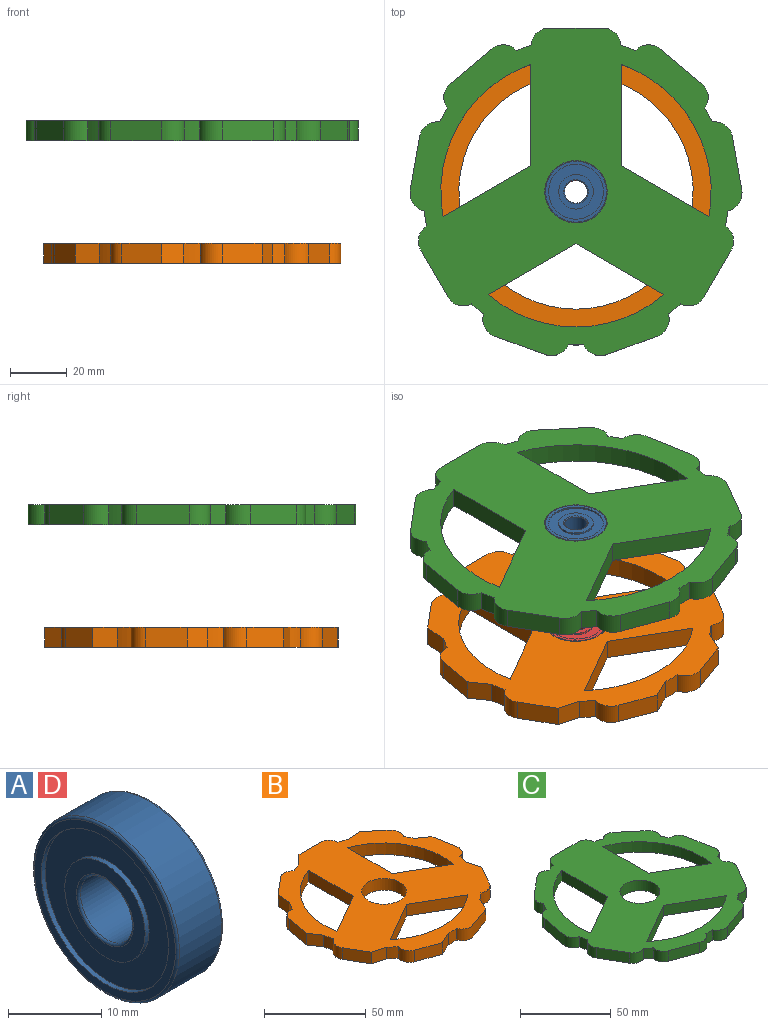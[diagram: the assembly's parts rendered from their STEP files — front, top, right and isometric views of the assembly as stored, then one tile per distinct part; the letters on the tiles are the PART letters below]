
ASSEMBLY  parts=4 mates=5
PART A: 16 faces, bbox 7x23.8x23.8 mm
  f0: torus R=10.7mm, axis (1,0,0), area 32.2mm2, adj f1,f15
  f1: plane 21.4x21.4mm, normal (-1,0,0), area 67.1mm2, adj f0,f2
  f2: cylinder r=9.65mm len=19.3mm, axis (1,0,0), area 36.4mm2, adj f1,f3
  f3: plane 19.3x19.3mm, normal (-1,0,0), area 175.7mm2, adj f2,f4
  f4: cylinder r=6.1mm len=12.2mm, axis (1,0,0), area 23mm2, adj f3,f5
  f5: plane 12.2x12.2mm, normal (-1,0,0), area 58.8mm2, adj f4,f6
  f6: torus R=4.3mm, axis (1,0,0), area 12.2mm2, adj f5,f7
  f7: cylinder r=4mm len=8mm, axis (1,0,0), area 160.8mm2, adj f6,f8
  f8: torus R=4.3mm, axis (1,0,0), area 12.2mm2, adj f7,f9
  f9: plane 12.2x12.2mm, normal (1,0,0), area 58.8mm2, adj f8,f10
  f10: cylinder r=6.1mm len=12.2mm, axis (1,0,0), area 23mm2, adj f9,f11
  f11: plane 19.3x19.3mm, normal (1,0,0), area 175.7mm2, adj f10,f12
  f12: cylinder r=9.65mm len=19.3mm, axis (1,0,0), area 36.4mm2, adj f11,f13
  f13: plane 21.4x21.4mm, normal (1,0,0), area 67.1mm2, adj f12,f14
  f14: torus R=10.7mm, axis (1,0,0), area 32.2mm2, adj f13,f15
  f15: cylinder r=11mm len=22mm, axis (1,0,0), area 442.3mm2, adj f0,f14
PART B: 48 faces, bbox 104.6x103.3x7 mm
  f0: plane 7.82x7mm, normal (0.91,-0.42,0), area 60.4mm2, adj f1,f41,f46,f47
  f1: cylinder r=47.62mm len=7mm, axis (0,0,-1), area 40.2mm2, adj f0,f2,f46,f47
  f2: cylinder r=6.1mm len=8.33mm, axis (0,0,-1), area 67.1mm2, adj f1,f3,f46,f47
  f3: plane 12.93x7.46mm, normal (0.87,-0.5,0), area 104.5mm2, adj f2,f4,f46,f47
  f4: plane 8.33x7mm, normal (0.97,0.26,0), area 60.4mm2, adj f3,f5,f46,f47
  f5: cylinder r=47.62mm len=7mm, axis (0,0,-1), area 40.2mm2, adj f4,f6,f46,f47
  f6: cylinder r=6.1mm len=7.07mm, axis (0,0,-1), area 67.1mm2, adj f5,f7,f46,f47
  f7: plane 14.7x7mm, normal (0.98,0.17,0), area 104.5mm2, adj f6,f8,f46,f47
  f8: plane 7.07x7mm, normal (0.57,0.82,0), area 60.4mm2, adj f7,f9,f46,f47
  f9: cylinder r=47.62mm len=7mm, axis (0,0,-1), area 40.2mm2, adj f8,f10,f46,f47
  f10: cylinder r=6.1mm len=8.59mm, axis (0,0,-1), area 67.1mm2, adj f9,f11,f46,f47
  f11: plane 11.44x9.6mm, normal (0.64,0.77,0), area 104.5mm2, adj f10,f12,f46,f47
  f12: plane 8.59x7mm, normal (-0.09,1,0), area 60.4mm2, adj f11,f13,f46,f47
  f13: cylinder r=47.62mm len=7mm, axis (0,0,-1), area 40.2mm2, adj f12,f14,f46,f47
  f14: cylinder r=6.1mm len=7mm, axis (0,0,-1), area 67.1mm2, adj f13,f15,f46,f47
  f15: plane 14.93x7mm, normal (0,1,0), area 104.5mm2, adj f14,f16,f46,f47
  f16: plane 7x6.1mm, normal (-0.71,0.71,0), area 60.4mm2, adj f15,f17,f46,f47
  f17: cylinder r=47.62mm len=7mm, axis (0,0,-1), area 40.2mm2, adj f16,f18,f46,f47
  f18: cylinder r=6.1mm len=8.59mm, axis (0,0,-1), area 67.1mm2, adj f17,f19,f46,f47
  f19: plane 11.44x9.6mm, normal (-0.64,0.77,0), area 104.5mm2, adj f18,f20,f46,f47
  f20: plane 8.59x7mm, normal (-1,0.09,0), area 60.4mm2, adj f19,f21,f46,f47
  f21: cylinder r=47.62mm len=7mm, axis (0,0,-1), area 40.2mm2, adj f20,f22,f46,f47
  f22: cylinder r=6.1mm len=7.07mm, axis (0,0,-1), area 67.1mm2, adj f21,f23,f46,f47
  f23: plane 14.7x7mm, normal (-0.98,0.17,0), area 104.5mm2, adj f22,f24,f46,f47
  f24: plane 7.07x7mm, normal (-0.82,-0.57,0), area 60.4mm2, adj f23,f25,f46,f47
  f25: cylinder r=47.62mm len=7mm, axis (0,0,-1), area 40.2mm2, adj f24,f26,f46,f47
  f26: cylinder r=6.1mm len=8.33mm, axis (0,0,-1), area 67.1mm2, adj f25,f27,f46,f47
  f27: plane 12.93x7.46mm, normal (-0.87,-0.5,0), area 104.5mm2, adj f26,f28,f46,f47
  f28: plane 8.33x7mm, normal (-0.26,-0.97,0), area 60.4mm2, adj f27,f29,f46,f47
  f29: cylinder r=47.62mm len=7mm, axis (0,0,-1), area 40.2mm2, adj f28,f30,f46,f47
  f30: cylinder r=6.1mm len=7.82mm, axis (0,0,-1), area 67.1mm2, adj f29,f31,f46,f47
  f31: plane 14.03x7mm, normal (-0.34,-0.94,0), area 104.5mm2, adj f30,f32,f46,f47
  f32: plane 7.82x7mm, normal (0.42,-0.91,0), area 60.4mm2, adj f31,f33,f46,f47
  f33: cylinder r=47.62mm len=7mm, axis (0,0,-1), area 40.2mm2, adj f32,f34,f46,f47
  f34: cylinder r=6.1mm len=7.82mm, axis (0,0,-1), area 67.1mm2, adj f33,f41,f46,f47
  f35: plane 26.98x15.58mm, normal (-0.5,0.87,0), area 218.1mm2, adj f36,f42,f46,f47
  f36: cylinder r=41.27mm len=46.73mm, axis (0,0,-1), area 411.6mm2, adj f35,f42,f46,f47
  f37: cylinder r=41.27mm len=53.96mm, axis (0,0,-1), area 411.6mm2, adj f38,f43,f46,f47
  f38: plane 26.98x15.58mm, normal (0.5,-0.87,0), area 218.1mm2, adj f37,f43,f46,f47
  f39: cylinder r=41.27mm len=46.73mm, axis (0,0,-1), area 411.6mm2, adj f40,f44,f46,f47
  f40: plane 26.98x15.58mm, normal (0.5,0.87,0), area 218.1mm2, adj f39,f44,f46,f47
  f41: plane 14.03x7mm, normal (0.34,-0.94,0), area 104.5mm2, adj f0,f34,f46,f47
  f42: plane 31.15x7mm, normal (-1,0,0), area 218.1mm2, adj f35,f36,f46,f47
  f43: plane 26.98x15.58mm, normal (-0.5,-0.87,0), area 218.1mm2, adj f37,f38,f46,f47
  f44: plane 31.15x7mm, normal (1,0,0), area 218.1mm2, adj f39,f40,f46,f47
  f45: cylinder r=11mm len=22mm, axis (0,0,-1), area 483.8mm2, adj f46,f47
  f46: plane 104.62x103.3mm, normal (0,0,1), area 5299.8mm2, adj f0,f1,f2,f3,f4,f5,f6,f7
  f47: plane 104.62x103.3mm, normal (0,0,-1), area 5299.8mm2, adj f0,f1,f2,f3,f4,f5,f6,f7
PART C: 48 faces, bbox 117x115.4x7 mm
  f0: cylinder r=47.62mm len=61.9mm, axis (0,0,-1), area 471.6mm2, adj f1,f41,f46,f47
  f1: plane 30.95x17.87mm, normal (0.5,-0.87,0), area 250.2mm2, adj f0,f41,f46,f47
  f2: cylinder r=47.62mm len=53.6mm, axis (0,0,-1), area 471.6mm2, adj f3,f42,f46,f47
  f3: plane 35.74x7mm, normal (-1,0,0), area 250.2mm2, adj f2,f42,f46,f47
  f4: cylinder r=47.62mm len=53.6mm, axis (0,0,-1), area 471.6mm2, adj f5,f43,f46,f47
  f5: plane 30.95x17.87mm, normal (0.5,0.87,0), area 250.2mm2, adj f4,f43,f46,f47
  f6: cylinder r=6.35mm len=8.72mm, axis (0,0,-1), area 67.4mm2, adj f7,f44,f46,f47
  f7: cylinder r=53.98mm len=7mm, axis (0,0,-1), area 38.3mm2, adj f6,f8,f46,f47
  f8: cylinder r=6.35mm len=7mm, axis (0,0,-1), area 67.4mm2, adj f7,f9,f46,f47
  f9: plane 19.05x7mm, normal (0,1,0), area 133.4mm2, adj f8,f10,f46,f47
  f10: cylinder r=6.35mm len=7mm, axis (0,0,-1), area 67.4mm2, adj f9,f11,f46,f47
  f11: cylinder r=53.98mm len=7mm, axis (0,0,-1), area 38.3mm2, adj f10,f12,f46,f47
  f12: cylinder r=6.35mm len=8.72mm, axis (0,0,-1), area 67.4mm2, adj f11,f13,f46,f47
  f13: plane 14.59x12.25mm, normal (-0.64,0.77,0), area 133.4mm2, adj f12,f14,f46,f47
  f14: cylinder r=6.35mm len=8.68mm, axis (0,0,-1), area 67.4mm2, adj f13,f15,f46,f47
  f15: cylinder r=53.98mm len=7mm, axis (0,0,-1), area 38.3mm2, adj f14,f16,f46,f47
  f16: cylinder r=6.35mm len=7.02mm, axis (0,0,-1), area 67.4mm2, adj f15,f17,f46,f47
  f17: plane 18.76x7mm, normal (-0.98,0.17,0), area 133.3mm2, adj f16,f18,f46,f47
  f18: cylinder r=6.35mm len=7.29mm, axis (0,0,-1), area 67.4mm2, adj f17,f19,f46,f47
  f19: cylinder r=53.98mm len=7mm, axis (0,0,-1), area 38.3mm2, adj f18,f20,f46,f47
  f20: cylinder r=6.35mm len=8.5mm, axis (0,0,-1), area 67.4mm2, adj f19,f21,f46,f47
  f21: plane 16.5x9.53mm, normal (-0.87,-0.5,0), area 133.4mm2, adj f20,f22,f46,f47
  f22: cylinder r=6.35mm len=8.38mm, axis (0,0,-1), area 67.4mm2, adj f21,f23,f46,f47
  f23: cylinder r=53.98mm len=7mm, axis (0,0,-1), area 38.3mm2, adj f22,f24,f46,f47
  f24: cylinder r=6.35mm len=7.82mm, axis (0,0,-1), area 67.4mm2, adj f23,f25,f46,f47
  f25: plane 17.9x7mm, normal (-0.34,-0.94,0), area 133.3mm2, adj f24,f26,f46,f47
  f26: cylinder r=6.35mm len=8.01mm, axis (0,0,-1), area 67.4mm2, adj f25,f27,f46,f47
  f27: cylinder r=53.98mm len=7mm, axis (0,0,-1), area 38.3mm2, adj f26,f28,f46,f47
  f28: cylinder r=6.35mm len=8.01mm, axis (0,0,-1), area 67.4mm2, adj f27,f29,f46,f47
  f29: plane 17.9x7mm, normal (0.34,-0.94,0), area 133.3mm2, adj f28,f30,f46,f47
  f30: cylinder r=6.35mm len=7.82mm, axis (0,0,-1), area 67.4mm2, adj f29,f31,f46,f47
  f31: cylinder r=53.98mm len=7mm, axis (0,0,-1), area 38.3mm2, adj f30,f32,f46,f47
  f32: cylinder r=6.35mm len=8.38mm, axis (0,0,-1), area 67.4mm2, adj f31,f33,f46,f47
  f33: plane 16.5x9.53mm, normal (0.87,-0.5,0), area 133.4mm2, adj f32,f34,f46,f47
  f34: cylinder r=6.35mm len=8.5mm, axis (0,0,-1), area 67.4mm2, adj f33,f35,f46,f47
  f35: cylinder r=53.98mm len=7mm, axis (0,0,-1), area 38.3mm2, adj f34,f36,f46,f47
  f36: cylinder r=6.35mm len=7.29mm, axis (0,0,-1), area 67.4mm2, adj f35,f37,f46,f47
  f37: plane 18.76x7mm, normal (0.98,0.17,0), area 133.3mm2, adj f36,f38,f46,f47
  f38: cylinder r=6.35mm len=7.02mm, axis (0,0,-1), area 67.4mm2, adj f37,f39,f46,f47
  f39: cylinder r=53.98mm len=7mm, axis (0,0,-1), area 38.3mm2, adj f38,f40,f46,f47
  f40: cylinder r=6.35mm len=8.68mm, axis (0,0,-1), area 67.4mm2, adj f39,f44,f46,f47
  f41: plane 30.95x17.87mm, normal (-0.5,-0.87,0), area 250.2mm2, adj f0,f1,f46,f47
  f42: plane 30.95x17.87mm, normal (-0.5,0.87,0), area 250.2mm2, adj f2,f3,f46,f47
  f43: plane 35.74x7mm, normal (1,0,0), area 250.2mm2, adj f4,f5,f46,f47
  f44: plane 14.59x12.25mm, normal (0.64,0.77,0), area 133.4mm2, adj f6,f40,f46,f47
  f45: cylinder r=11mm len=22mm, axis (0,0,-1), area 483.8mm2, adj f46,f47
  f46: plane 116.95x115.37mm, normal (0,0,1), area 6766.8mm2, adj f0,f1,f2,f3,f4,f5,f6,f7
  f47: plane 116.95x115.37mm, normal (0,0,-1), area 6766.8mm2, adj f0,f1,f2,f3,f4,f5,f6,f7
PART D: same geometry as A
PLACE A rot(axis=(0,1,0),90deg) t=(-16.96,25.75,50.39)mm
PLACE B t=(-16.96,25.75,0.12)mm
PLACE C t=(-16.96,25.75,43.39)mm
PLACE D rot(axis=(0,1,0),90deg) t=(-16.96,25.75,7.12)mm
MATE cylindrical D.f0 <-> A.f0  axis (0,0,-1) through (-16.96,25.75,3.62)mm
MATE planar B.f45 <-> D.f0  axis (0,0,1) through (-16.96,25.75,7.12)mm
MATE planar C.f0 <-> A.f0  axis (0,0,1) through (-16.96,25.75,50.39)mm
MATE cylindrical D.f0 <-> B.f45  axis (0,0,-1) through (-16.96,25.75,6.82)mm
MATE cylindrical A.f0 <-> C.f0  axis (0,0,-1) through (-16.96,25.75,46.89)mm
